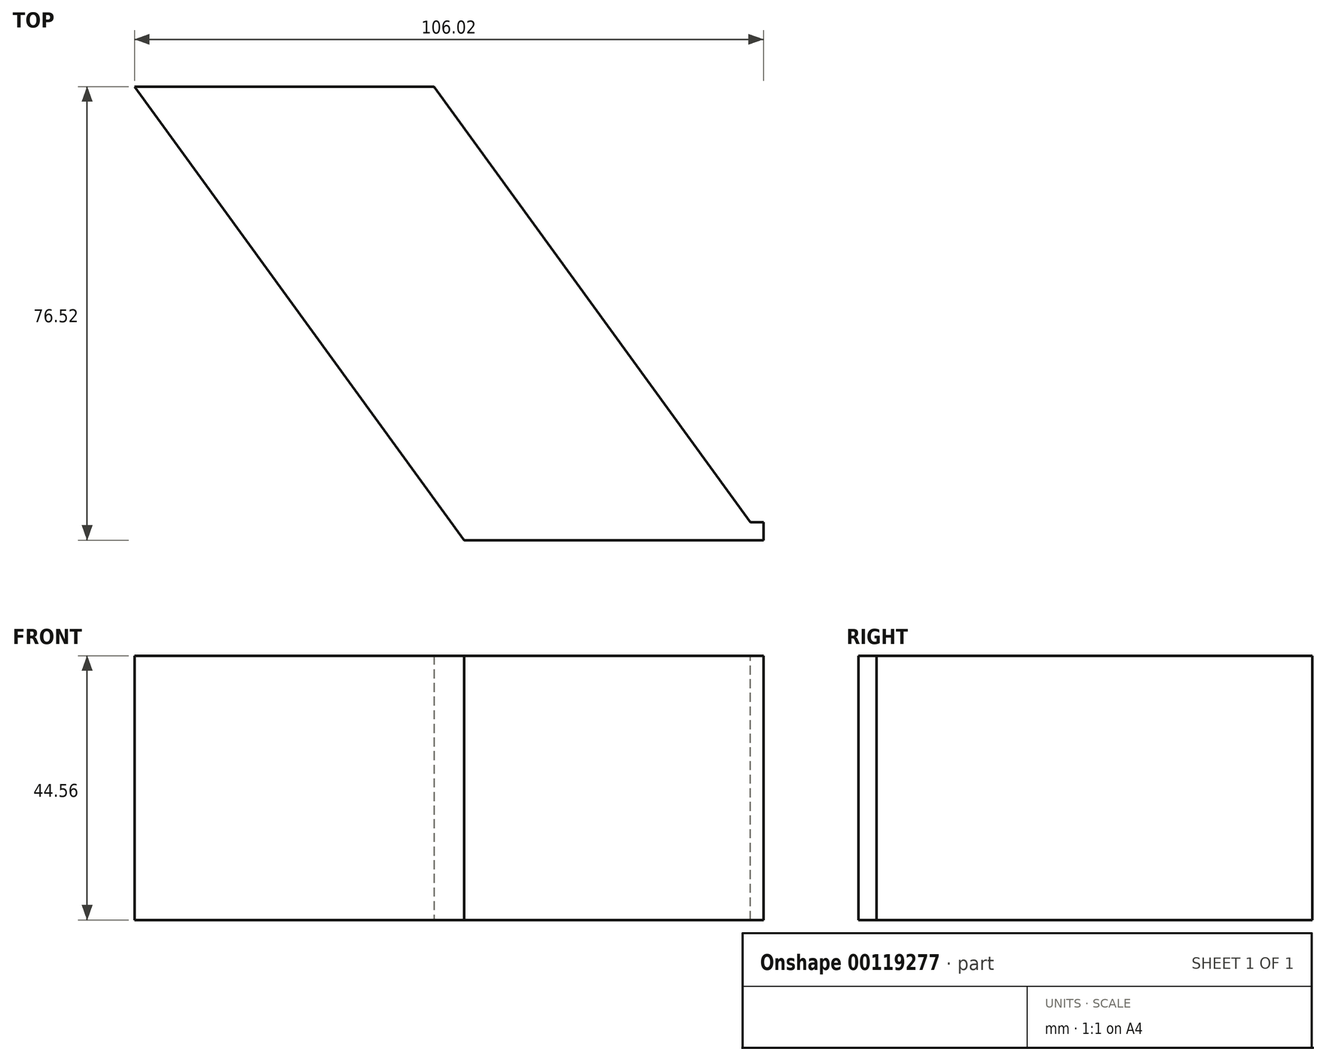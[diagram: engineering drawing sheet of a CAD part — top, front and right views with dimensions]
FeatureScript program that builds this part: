
annotation { "Feature Type Name" : "Feature", "Feature Type Description" : "" }
export const myFeature = defineFeature(function(context is Context, id is Id, definition is map)
    precondition{}
    {
        {
            var Q0;
            Q0=qCreatedBy(makeId("Front.planeOp"),FACE);
            var sketch = newSketch(context, id + "F0", { "sketchPlane" : qUnion([Q0])});
            skLineSegment(sketch, "E0.bottom", {"start": v(24.62, 29.3) * mm, "end": v(-25.84, 29.3) * mm});
            skLineSegment(sketch, "E0.top", {"start": v(24.62, -15.26) * mm, "end": v(-25.84, -15.26) * mm});
            skLineSegment(sketch, "E0.left", {"start": v(24.62, 29.3) * mm, "end": v(24.62, -15.26) * mm});
            skLineSegment(sketch, "E0.right", {"start": v(-25.84, 29.3) * mm, "end": v(-25.84, -15.26) * mm});
            skSolve(sketch);
        }
        {
            var Q0;
            Q0 = qSketchRegion(id + "F0", true);
            var Q1;
            Q1=makeQuery(id+"F0.imprint","IMPRINT",FACE,{"disambiguationData":[TD([[makeQuery(id+"F0.imprint","IMPRINT",EDGE,{"derivedFrom":sQuery(id+"F0.wireOp",EDGE,"E0.bottom")}),1.0]])]});
            extrude(context, id + "F1", {"entities" : qUnion([Q0, Q1]), "depth" : 3.05 * mm});
        }
        {
            var Q0;
            Q0=qCreatedBy(makeId("Top.planeOp"),FACE);
            var sketch = newSketch(context, id + "F2", { "sketchPlane" : qUnion([Q0])});
            skLineSegment(sketch, "E1", {"start": v(-55.55, 76.51) * mm, "end": v(0, 0) * mm});
            skSolve(sketch);
        }
        {
            var Q0;
            Q0=makeQuery(id+"F1.opExtrude","CAP_FACE",FACE,{"disambiguationData":[OSD([sQuery(id+"F0.wireOp",EDGE,"E0.bottom"),sQuery(id+"F0.wireOp",EDGE,"E0.top"),sQuery(id+"F0.wireOp",EDGE,"E0.left"),sQuery(id+"F0.wireOp",EDGE,"E0.right")])],"isStart":false});
            var Q1;
            Q1=sQuery(id+"F2.wireOp",EDGE,"E1");
            sweep(context, id + "F3", {"operationType" : NewBodyOperationType.ADD, "profiles" : qUnion([Q0]), "path" : qUnion([Q1])});
        }
    });
